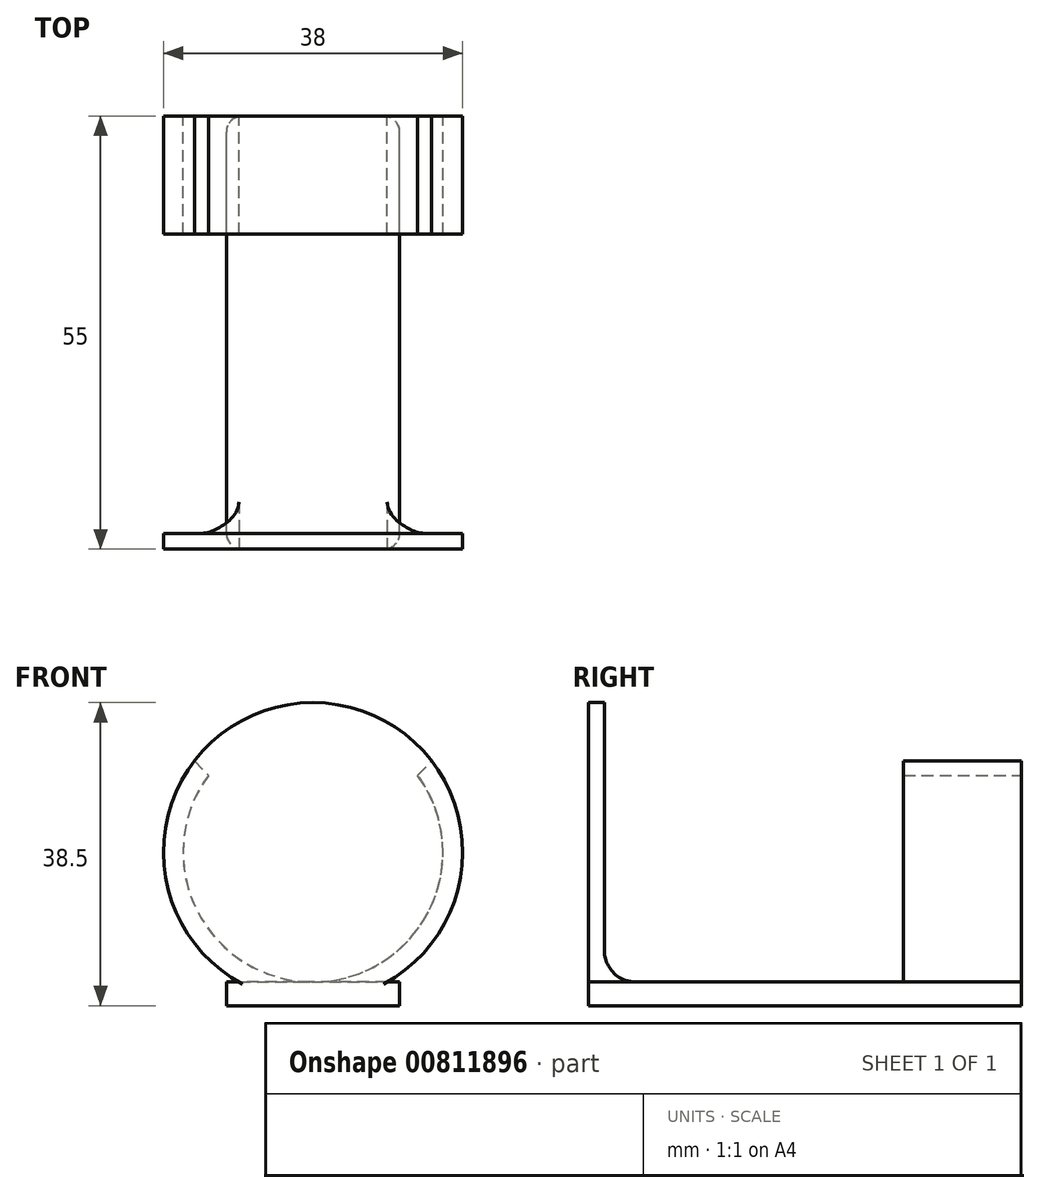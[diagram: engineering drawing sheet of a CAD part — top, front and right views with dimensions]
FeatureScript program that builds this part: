
annotation { "Feature Type Name" : "Feature", "Feature Type Description" : "" }
export const myFeature = defineFeature(function(context is Context, id is Id, definition is map)
    precondition{}
    {
        {
            var Q0;
            Q0=qCreatedBy(makeId("Top.planeOp"),FACE);
            var sketch = newSketch(context, id + "F0", { "sketchPlane" : qUnion([Q0])});
            skLineSegment(sketch, "E0.bottom", {"start": v(11, -27.5) * mm, "end": v(-11, -27.5) * mm});
            skLineSegment(sketch, "E0.top", {"start": v(11, 27.5) * mm, "end": v(-11, 27.5) * mm});
            skLineSegment(sketch, "E0.left", {"start": v(11, -27.5) * mm, "end": v(11, 27.5) * mm});
            skLineSegment(sketch, "E0.right", {"start": v(-11, -27.5) * mm, "end": v(-11, 27.5) * mm});
            skPoint(sketch, "E0.middle", {"position": v(0, 0) * mm});
            skSolve(sketch);
        }
        {
            var Q0;
            Q0=makeQuery(id+"F0.imprint","IMPRINT",FACE,{"disambiguationData":[TD([[makeQuery(id+"F0.imprint","IMPRINT",EDGE,{"derivedFrom":sQuery(id+"F0.wireOp",EDGE,"E0.bottom")}),-1.0]])]});
            extrude(context, id + "F1", {"entities" : qUnion([Q0]), "depth" : 3 * mm, "offsetDistance" : 25 * mm});
        }
        {
            var Q0;
            Q0=makeQuery(id+"F1.opExtrude","SWEPT_EDGE",EDGE,{"disambiguationData":[OSD([sQuery(id+"F0.wireOp",EDGE,"E0.top"),sQuery(id+"F0.wireOp",EDGE,"E0.right")])]});
            var Q1;
            Q1=makeQuery(id+"F1.opExtrude","SWEPT_EDGE",EDGE,{"disambiguationData":[OSD([sQuery(id+"F0.wireOp",EDGE,"E0.top"),sQuery(id+"F0.wireOp",EDGE,"E0.left")])]});
            var Q2;
            Q2=makeQuery(id+"F1.opExtrude","SWEPT_EDGE",EDGE,{"disambiguationData":[OSD([sQuery(id+"F0.wireOp",EDGE,"E0.bottom"),sQuery(id+"F0.wireOp",EDGE,"E0.left")])]});
            var Q3;
            Q3=makeQuery(id+"F1.opExtrude","SWEPT_EDGE",EDGE,{"disambiguationData":[OSD([sQuery(id+"F0.wireOp",EDGE,"E0.bottom"),sQuery(id+"F0.wireOp",EDGE,"E0.right")])]});
            fillet(context, id + "F2", {"entities" : qUnion([Q0, Q1, Q2, Q3]), "radius" : 2 * mm, "tangentPropagation" : true, "allowEdgeOverflow" : false});
        }
        {
            var Q0;
            Q0=makeQuery(id+"F1.opExtrude","SWEPT_FACE",FACE,{"disambiguationData":[OSD([sQuery(id+"F0.wireOp",EDGE,"E0.bottom")])]});
            var sketch = newSketch(context, id + "F3", { "sketchPlane" : qUnion([Q0])});
            skCircle(sketch, "E1", {"center": v(0, 19.5) * mm, "radius": 16.5 * mm});
            skCircle(sketch, "E2", {"center": v(0, 19.5) * mm, "radius": 19 * mm});
            skSolve(sketch);
        }
        {
            var Q0;
            {var subQ10=sQuery(id+"F3.wireOp",EDGE,"E1");Q0=makeQuery(id+"F3.imprint","IMPRINT",FACE,{"disambiguationData":[TD([[makeQuery(id+"F3.imprint","IMPRINT",EDGE,{"derivedFrom":subQ10}),-1.0]])]});}
            var Q1;
            Q1=makeQuery(id+"F3.imprint","IMPRINT",FACE,{"disambiguationData":[TD([[makeQuery(id+"F3.imprint","IMPRINT",EDGE,{"derivedFrom":sQuery(id+"F3.wireOp",EDGE,"E1")}),1.0]])]});
            extrude(context, id + "F4", {"entities" : qUnion([Q0, Q1]), "operationType" : NewBodyOperationType.ADD, "oppositeDirection" : true, "depth" : 2 * mm, "offsetDistance" : 25 * mm});
        }
        {
            var Q0;
            {var subQ0=sQuery(id+"F0.wireOp",EDGE,"E0.right");var subQ1=sQuery(id+"F0.wireOp",EDGE,"E0.left");var subQ2=sQuery(id+"F0.wireOp",EDGE,"E0.bottom");Q0=makeQuery(id+"F4.boolean.opBoolean","INTERSECT",EDGE,{"derivedFrom":[makeQuery(id+"F1.opExtrude","CAP_FACE",FACE,{"disambiguationData":[OSD([subQ2,sQuery(id+"F0.wireOp",EDGE,"E0.top"),subQ1,subQ0])],"isStart":false}),makeQuery(id+"F4.opExtrude","CAP_FACE",FACE,{"disambiguationData":[OSD([subQ2,subQ1,subQ0,sQuery(id+"F3.wireOp",EDGE,"E2")])],"isStart":false})]});}
            fillet(context, id + "F5", {"entities" : qUnion([Q0]), "radius" : 4 * mm, "tangentPropagation" : true, "allowEdgeOverflow" : false});
        }
        {
            var Q0;
            Q0=makeQuery(id+"F1.opExtrude","SWEPT_FACE",FACE,{"disambiguationData":[OSD([sQuery(id+"F0.wireOp",EDGE,"E0.top")])]});
            var sketch = newSketch(context, id + "F6", { "sketchPlane" : qUnion([Q0])});
            skCircle(sketch, "E3", {"center": v(0, 19.5) * mm, "radius": 16.5 * mm});
            skCircle(sketch, "E4", {"center": v(0, 19.5) * mm, "radius": 19 * mm});
            skSolve(sketch);
        }
        {
            var Q0;
            Q0 = qSketchRegion(id + "F6", true);
            extrude(context, id + "F7", {"entities" : qUnion([Q0]), "operationType" : NewBodyOperationType.ADD, "oppositeDirection" : true, "depth" : 15 * mm, "offsetDistance" : 25 * mm});
        }
        {
            var Q0;
            Q0=makeQuery(id+"F7.boolean.opBoolean","MERGE",FACE,{"derivedFrom":[makeQuery(id+"F1.opExtrude","SWEPT_FACE",FACE,{"disambiguationData":[OSD([sQuery(id+"F0.wireOp",EDGE,"E0.top")])]}),makeQuery(id+"F7.opExtrude","CAP_FACE",FACE,{"disambiguationData":[OSD([sQuery(id+"F6.wireOp",EDGE,"E3"),sQuery(id+"F6.wireOp",EDGE,"E4")])],"isStart":true})]});
            var sketch = newSketch(context, id + "F8", { "sketchPlane" : qUnion([Q0])});
            skLineSegment(sketch, "E5", {"start": v(0, 26.49) * mm, "end": v(-10.5, 26.49) * mm});
            skLineSegment(sketch, "E6", {"start": v(-10.5, 26.49) * mm, "end": v(-23.23, 39.22) * mm});
            skLineSegment(sketch, "E7", {"start": v(-23.23, 39.22) * mm, "end": v(23.23, 39.22) * mm});
            skLineSegment(sketch, "E8", {"start": v(23.23, 39.22) * mm, "end": v(10.5, 26.49) * mm});
            skLineSegment(sketch, "E9", {"start": v(10.5, 26.49) * mm, "end": v(0, 26.49) * mm});
            skSolve(sketch);
        }
        {
            var Q0;
            Q0 = qSketchRegion(id + "F8", true);
            extrude(context, id + "F9", {"entities" : qUnion([Q0]), "operationType" : NewBodyOperationType.REMOVE, "oppositeDirection" : true, "depth" : 25 * mm, "offsetDistance" : 25 * mm});
        }
    });
